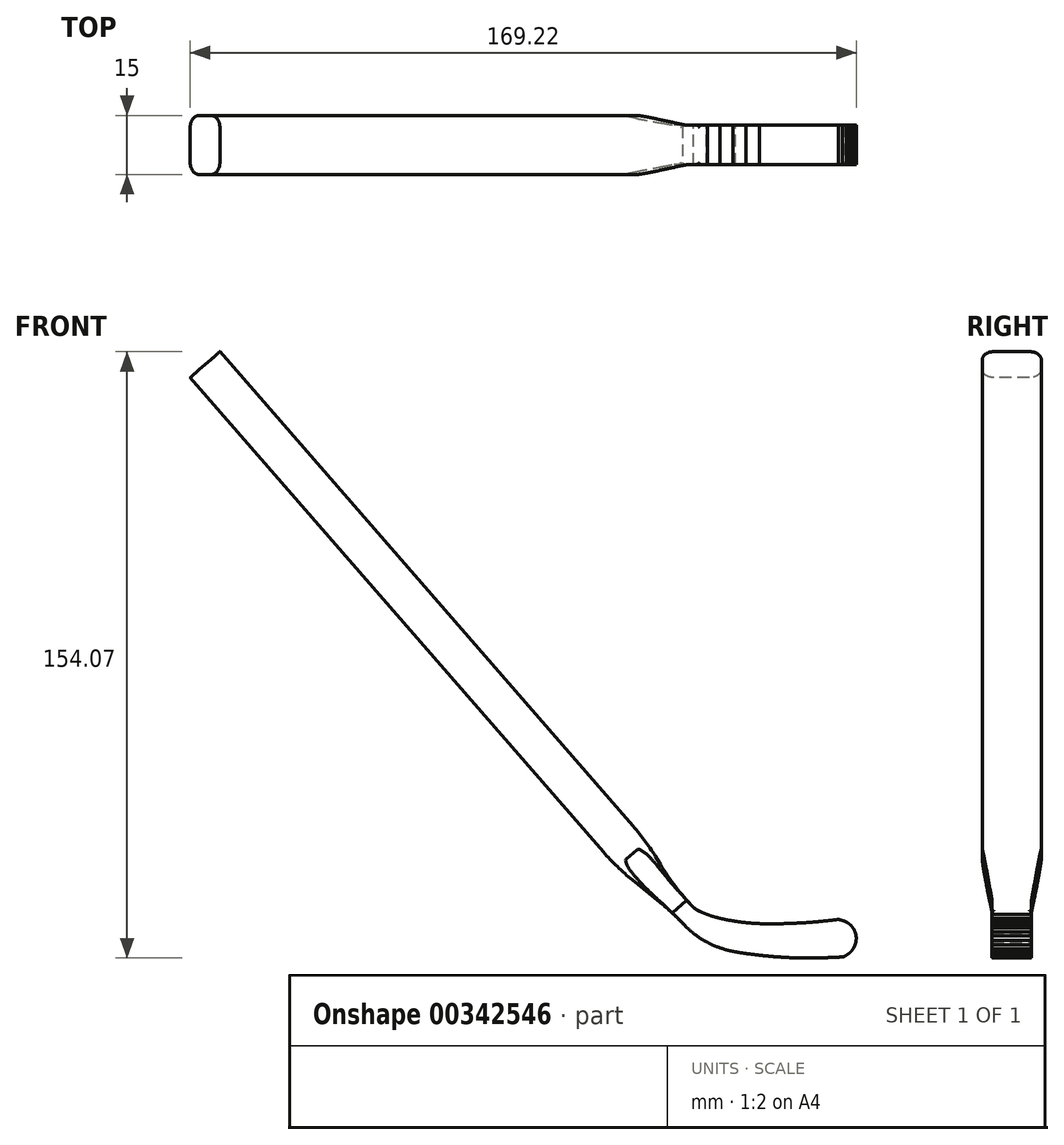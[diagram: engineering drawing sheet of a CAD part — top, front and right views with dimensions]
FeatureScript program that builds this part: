
annotation { "Feature Type Name" : "Feature", "Feature Type Description" : "" }
export const myFeature = defineFeature(function(context is Context, id is Id, definition is map)
    precondition{}
    {
        {
            var Q0;
            Q0=qCreatedBy(makeId("Front.planeOp"),FACE);
            var sketch = newSketch(context, id + "F0", { "sketchPlane" : qUnion([Q0])});
            skFitSpline(sketch, "E0.0", {"points": [v(-96.58, 20.1) * mm, v(-97.72, 20.03) * mm, v(-98.88, 19.98) * mm, v(-100.04, 19.94) * mm]});
            skFitSpline(sketch, "E1.0", {"points": [v(-93.22, 20.32) * mm, v(-94.31, 20.23) * mm, v(-95.44, 20.15) * mm, v(-96.58, 20.1) * mm]});
            skFitSpline(sketch, "E2.0", {"points": [v(-90.02, 20.62) * mm, v(-91.06, 20.51) * mm, v(-92.12, 20.4) * mm, v(-93.22, 20.32) * mm]});
            skFitSpline(sketch, "E3.0", {"points": [v(-86.91, 20.97) * mm, v(-87.3, 20.93) * mm, v(-87.69, 20.88) * mm, v(-88.72, 20.77) * mm, v(-89.5, 20.68) * mm, v(-90.02, 20.62) * mm]});
            skFitSpline(sketch, "E4.0", {"points": [v(-123.3, 23.6) * mm, v(-123.8, 23.85) * mm, v(-124.54, 24.24) * mm, v(-125.52, 24.78) * mm, v(-125.9, 24.98) * mm, v(-126.26, 25.18) * mm]});
            skFitSpline(sketch, "E5.0", {"points": [v(-120.24, 22.25) * mm, v(-121.28, 22.64) * mm, v(-122.3, 23.1) * mm, v(-123.3, 23.6) * mm]});
            skFitSpline(sketch, "E6.0", {"points": [v(-117.03, 21.27) * mm, v(-118.12, 21.54) * mm, v(-119.2, 21.85) * mm, v(-120.24, 22.25) * mm]});
            skFitSpline(sketch, "E7.0", {"points": [v(-113.73, 20.61) * mm, v(-114.84, 20.8) * mm, v(-115.94, 21) * mm, v(-117.03, 21.27) * mm]});
            skFitSpline(sketch, "E8.0", {"points": [v(-110.37, 20.17) * mm, v(-111.5, 20.28) * mm, v(-112.61, 20.43) * mm, v(-113.73, 20.61) * mm]});
            skFitSpline(sketch, "E9.0", {"points": [v(-106.97, 19.92) * mm, v(-108.11, 19.97) * mm, v(-109.25, 20.05) * mm, v(-110.37, 20.17) * mm]});
            skFitSpline(sketch, "E10.0", {"points": [v(-103.52, 19.86) * mm, v(-104.68, 19.86) * mm, v(-105.83, 19.87) * mm, v(-106.97, 19.92) * mm]});
            skFitSpline(sketch, "E11.0", {"points": [v(-100.04, 19.94) * mm, v(-101.2, 19.9) * mm, v(-102.36, 19.87) * mm, v(-103.52, 19.86) * mm]});
            skFitSpline(sketch, "E12.0", {"points": [v(-93.11, 11.2) * mm, v(-91.83, 11.2) * mm, v(-90.58, 11.24) * mm, v(-89.35, 11.29) * mm]});
            skFitSpline(sketch, "E13.0", {"points": [v(-89.35, 11.29) * mm, v(-88.73, 11.3) * mm, v(-87.82, 11.35) * mm, v(-86.6, 11.4) * mm, v(-86.15, 11.42) * mm, v(-85.7, 11.44) * mm]});
            skFitSpline(sketch, "E14.0", {"points": [v(-97.05, 11.21) * mm, v(-95.71, 11.18) * mm, v(-94.4, 11.18) * mm, v(-93.11, 11.2) * mm]});
            skFitSpline(sketch, "E15.0", {"points": [v(-101.09, 11.38) * mm, v(-99.73, 11.3) * mm, v(-98.38, 11.24) * mm, v(-97.05, 11.21) * mm]});
            skFitSpline(sketch, "E16.0", {"points": [v(-105.14, 11.7) * mm, v(-103.8, 11.57) * mm, v(-102.44, 11.46) * mm, v(-101.09, 11.38) * mm]});
            skFitSpline(sketch, "E17.0", {"points": [v(-109.17, 12.15) * mm, v(-107.84, 11.98) * mm, v(-106.5, 11.83) * mm, v(-105.14, 11.7) * mm]});
            skFitSpline(sketch, "E18.0", {"points": [v(-113.12, 12.76) * mm, v(-111.83, 12.5) * mm, v(-110.5, 12.32) * mm, v(-109.17, 12.15) * mm]});
            skFitSpline(sketch, "E19.0", {"points": [v(-116.92, 13.73) * mm, v(-115.7, 13.32) * mm, v(-114.42, 13) * mm, v(-113.12, 12.76) * mm]});
            skFitSpline(sketch, "E20.0", {"points": [v(-120.48, 15.3) * mm, v(-119.34, 14.68) * mm, v(-118.15, 14.15) * mm, v(-116.92, 13.73) * mm]});
            skFitSpline(sketch, "E21.0", {"points": [v(-123.73, 17.45) * mm, v(-122.7, 16.64) * mm, v(-121.62, 15.92) * mm, v(-120.48, 15.3) * mm]});
            skFitSpline(sketch, "E22.0", {"points": [v(-126.63, 20.09) * mm, v(-125.7, 19.15) * mm, v(-124.75, 18.26) * mm, v(-123.73, 17.45) * mm]});
            skFitSpline(sketch, "E23.0", {"points": [v(-129.33, 22.99) * mm, v(-129, 22.62) * mm, v(-128.66, 22.25) * mm, v(-127.77, 21.27) * mm, v(-127.09, 20.56) * mm, v(-126.63, 20.09) * mm]});
            skFitSpline(sketch, "E24.0", {"points": [v(-85.87, 20.69) * mm, v(-86.04, 20.74) * mm, v(-86.3, 20.81) * mm, v(-86.65, 20.9) * mm, v(-86.78, 20.94) * mm, v(-86.91, 20.97) * mm]});
            skFitSpline(sketch, "E25.0", {"points": [v(-84.88, 20.28) * mm, v(-85.2, 20.45) * mm, v(-85.53, 20.58) * mm, v(-85.87, 20.69) * mm]});
            skFitSpline(sketch, "E26.0", {"points": [v(-84, 19.66) * mm, v(-84.27, 19.9) * mm, v(-84.56, 20.11) * mm, v(-84.88, 20.28) * mm]});
            skFitSpline(sketch, "E27.0", {"points": [v(-83.27, 18.84) * mm, v(-83.48, 19.15) * mm, v(-83.73, 19.42) * mm, v(-84, 19.66) * mm]});
            skFitSpline(sketch, "E28.0", {"points": [v(-82.74, 17.86) * mm, v(-82.88, 18.21) * mm, v(-83.06, 18.54) * mm, v(-83.27, 18.84) * mm]});
            skFitSpline(sketch, "E29.0", {"points": [v(-82.46, 16.77) * mm, v(-82.51, 17.15) * mm, v(-82.6, 17.51) * mm, v(-82.74, 17.86) * mm]});
            skFitSpline(sketch, "E30.0", {"points": [v(-82.46, 15.65) * mm, v(-82.42, 16.02) * mm, v(-82.41, 16.4) * mm, v(-82.46, 16.77) * mm]});
            skFitSpline(sketch, "E31.0", {"points": [v(-82.72, 14.55) * mm, v(-82.6, 14.9) * mm, v(-82.5, 15.27) * mm, v(-82.46, 15.65) * mm]});
            skFitSpline(sketch, "E32.0", {"points": [v(-83.21, 13.54) * mm, v(-83.01, 13.85) * mm, v(-82.85, 14.2) * mm, v(-82.72, 14.55) * mm]});
            skFitSpline(sketch, "E33.0", {"points": [v(-83.9, 12.68) * mm, v(-83.65, 12.93) * mm, v(-83.41, 13.22) * mm, v(-83.21, 13.54) * mm]});
            skFitSpline(sketch, "E34.0", {"points": [v(-84.76, 12) * mm, v(-84.46, 12.2) * mm, v(-84.17, 12.43) * mm, v(-83.9, 12.68) * mm]});
            skFitSpline(sketch, "E35.0", {"points": [v(-85.7, 11.44) * mm, v(-85.57, 11.51) * mm, v(-85.45, 11.58) * mm, v(-85.14, 11.77) * mm, v(-84.9, 11.9) * mm, v(-84.76, 12) * mm]});
            skLineSegment(sketch, "E36", {"start": v(-126.26, 25.18) * mm, "end": v(-129.09, 22.72) * mm});
            skSolve(sketch);
        }
        {
            var Q0;
            Q0=makeQuery(id+"F0.imprint","IMPRINT",FACE,{"disambiguationData":[TD([[makeQuery(id+"F0.imprint","IMPRINT",EDGE,{"derivedFrom":sQuery(id+"F0.wireOp",EDGE,"E0.0")}),1.0]])]});
            extrude(context, id + "F1", {"entities" : qUnion([Q0]), "depth" : 10 * mm});
        }
        {
            var Q0;
            Q0=makeQuery(id+"F1.opExtrude","SWEPT_FACE",FACE,{"disambiguationData":[OSD([sQuery(id+"F0.wireOp",EDGE,"E36")])]});
            cPlane(context, id + "F2", {"entities" : qUnion([Q0]), "cplaneType" : CPlaneType.OFFSET, "offset" : 18 * mm, "width" : 150 * mm, "height" : 150 * mm});
        }
        {
            var Q0;
            Q0=qCreatedBy(id+"F2.planeOp",FACE);
            var sketch = newSketch(context, id + "F3", { "sketchPlane" : qUnion([Q0])});
            skLineSegment(sketch, "E37.0", {"start": v(-78.68, -10) * mm, "end": v(-78.68, 0) * mm});
            skLineSegment(sketch, "E38.0", {"start": v(-78.68, -10) * mm, "end": v(-82.43, -10) * mm, "construction": true});
            skPoint(sketch, "E39", {"position": v(-80.56, -5) * mm});
            skPoint(sketch, "E39.positionSnap0", {"position": v(-80.56, -10) * mm});
            skPoint(sketch, "E39.positionSnap1", {"position": v(-78.68, -5) * mm});
            skLineSegment(sketch, "E40.bottom", {"start": v(-75.56, 2.5) * mm, "end": v(-85.56, 2.5) * mm});
            skLineSegment(sketch, "E40.top", {"start": v(-75.56, -12.5) * mm, "end": v(-85.56, -12.5) * mm});
            skLineSegment(sketch, "E40.left", {"start": v(-75.56, 2.5) * mm, "end": v(-75.56, -12.5) * mm});
            skLineSegment(sketch, "E40.right", {"start": v(-85.56, 2.5) * mm, "end": v(-85.56, -12.5) * mm});
            skSolve(sketch);
        }
        {
            var Q0;
            Q0=makeQuery(id+"F3.imprint","IMPRINT",FACE,{"disambiguationData":[TD([[makeQuery(id+"F3.imprint","IMPRINT",EDGE,{"derivedFrom":sQuery(id+"F3.wireOp",EDGE,"E40.bottom")}),1.0]])]});
            extrude(context, id + "F4", {"entities" : qUnion([Q0]), "depth" : 165 * mm});
        }
        {
            var Q0;
            Q0=makeQuery(id+"F4.opExtrude","CAP_FACE",FACE,{"disambiguationData":[OSD([sQuery(id+"F3.wireOp",EDGE,"E40.bottom"),sQuery(id+"F3.wireOp",EDGE,"E40.top"),sQuery(id+"F3.wireOp",EDGE,"E40.left"),sQuery(id+"F3.wireOp",EDGE,"E40.right")])],"isStart":true});
            var Q1;
            Q1=makeQuery(id+"F1.opExtrude","SWEPT_FACE",FACE,{"disambiguationData":[OSD([sQuery(id+"F0.wireOp",EDGE,"E36")])]});
            loft(context, id + "F5", {"sheetProfilesArray" : [{ "sheetProfileEntities" : qUnion([Q0]) }, { "sheetProfileEntities" : qUnion([Q1]) }]});
        }
        {
            var Q0;
            Q0=makeQuery(id+"F1.opExtrude","SWEPT_BODY",BODY,{"disambiguationData":[OSD([sQuery(id+"F0.wireOp",EDGE,"E0.0"),sQuery(id+"F0.wireOp",EDGE,"E1.0"),sQuery(id+"F0.wireOp",EDGE,"E2.0"),sQuery(id+"F0.wireOp",EDGE,"E3.0"),sQuery(id+"F0.wireOp",EDGE,"E4.0"),sQuery(id+"F0.wireOp",EDGE,"E5.0"),sQuery(id+"F0.wireOp",EDGE,"E6.0"),sQuery(id+"F0.wireOp",EDGE,"E7.0"),sQuery(id+"F0.wireOp",EDGE,"E8.0"),sQuery(id+"F0.wireOp",EDGE,"E9.0"),sQuery(id+"F0.wireOp",EDGE,"E10.0"),sQuery(id+"F0.wireOp",EDGE,"E11.0"),sQuery(id+"F0.wireOp",EDGE,"E12.0"),sQuery(id+"F0.wireOp",EDGE,"E13.0"),sQuery(id+"F0.wireOp",EDGE,"E14.0"),sQuery(id+"F0.wireOp",EDGE,"E15.0"),sQuery(id+"F0.wireOp",EDGE,"E16.0"),sQuery(id+"F0.wireOp",EDGE,"E17.0"),sQuery(id+"F0.wireOp",EDGE,"E18.0"),sQuery(id+"F0.wireOp",EDGE,"E19.0"),sQuery(id+"F0.wireOp",EDGE,"E20.0"),sQuery(id+"F0.wireOp",EDGE,"E21.0"),sQuery(id+"F0.wireOp",EDGE,"E22.0"),sQuery(id+"F0.wireOp",EDGE,"E23.0"),sQuery(id+"F0.wireOp",EDGE,"E24.0"),sQuery(id+"F0.wireOp",EDGE,"E25.0"),sQuery(id+"F0.wireOp",EDGE,"E26.0"),sQuery(id+"F0.wireOp",EDGE,"E27.0"),sQuery(id+"F0.wireOp",EDGE,"E28.0"),sQuery(id+"F0.wireOp",EDGE,"E29.0"),sQuery(id+"F0.wireOp",EDGE,"E30.0"),sQuery(id+"F0.wireOp",EDGE,"E31.0"),sQuery(id+"F0.wireOp",EDGE,"E32.0"),sQuery(id+"F0.wireOp",EDGE,"E33.0"),sQuery(id+"F0.wireOp",EDGE,"E34.0"),sQuery(id+"F0.wireOp",EDGE,"E35.0"),sQuery(id+"F0.wireOp",EDGE,"E36")])]});
            var Q1;
            Q1=makeQuery(id+"F5.opLoft","SWEPT_BODY",BODY,{"disambiguationData":[OSD([sQuery(id+"F0.wireOp",EDGE,"E36"),sQuery(id+"F3.wireOp",EDGE,"E40.bottom"),sQuery(id+"F3.wireOp",EDGE,"E40.top"),sQuery(id+"F3.wireOp",EDGE,"E40.left"),sQuery(id+"F3.wireOp",EDGE,"E40.right")])]});
            var Q2;
            Q2=makeQuery(id+"F4.opExtrude","SWEPT_BODY",BODY,{"disambiguationData":[OSD([sQuery(id+"F3.wireOp",EDGE,"E40.bottom"),sQuery(id+"F3.wireOp",EDGE,"E40.top"),sQuery(id+"F3.wireOp",EDGE,"E40.left"),sQuery(id+"F3.wireOp",EDGE,"E40.right")])]});
            booleanBodies(context, id + "F6", {"operationType" : BooleanOperationType.UNION, "tools" : qUnion([Q0, Q1, Q2])});
        }
        {
            var Q0;
            {var subQ0=sQuery(id+"F0.wireOp",EDGE,"E36");var subQ1=sQuery(id+"F0.wireOp",EDGE,"E4.0");Q0=makeQuery(id+"F6.opBoolean","MERGE",EDGE,{"derivedFrom":[makeQuery(id+"F1.opExtrude","SWEPT_EDGE",EDGE,{"disambiguationData":[OSD([subQ1,subQ0])]}),makeQuery(id+"F5.opLoft","MID_CAP_EDGE",EDGE,{"disambiguationData":[OSD([subQ1,subQ0])],"capPos":1.0})]});}
            var Q1;
            {var subQ0=sQuery(id+"F3.wireOp",EDGE,"E40.left");Q1=makeQuery(id+"F6.opBoolean","MERGE",EDGE,{"derivedFrom":[makeQuery(id+"F4.opExtrude","CAP_EDGE",EDGE,{"disambiguationData":[OSD([subQ0])],"isStart":true}),makeQuery(id+"F5.opLoft","MID_CAP_EDGE",EDGE,{"disambiguationData":[OSD([sQuery(id+"F3.wireOp",EDGE,"E40.bottom"),sQuery(id+"F3.wireOp",EDGE,"E40.top"),subQ0])],"capPos":0.0})]});}
            var Q2;
            {var subQ0=sQuery(id+"F0.wireOp",EDGE,"E36");var subQ1=sQuery(id+"F0.wireOp",EDGE,"E23.0");Q2=makeQuery(id+"F6.opBoolean","MERGE",EDGE,{"derivedFrom":[makeQuery(id+"F1.opExtrude","SWEPT_EDGE",EDGE,{"disambiguationData":[OSD([subQ1,subQ0])]}),makeQuery(id+"F5.opLoft","MID_CAP_EDGE",EDGE,{"disambiguationData":[OSD([subQ1,subQ0])],"capPos":1.0})]});}
            var Q3;
            {var subQ0=sQuery(id+"F3.wireOp",EDGE,"E40.right");Q3=makeQuery(id+"F6.opBoolean","MERGE",EDGE,{"derivedFrom":[makeQuery(id+"F4.opExtrude","CAP_EDGE",EDGE,{"disambiguationData":[OSD([subQ0])],"isStart":true}),makeQuery(id+"F5.opLoft","MID_CAP_EDGE",EDGE,{"disambiguationData":[OSD([sQuery(id+"F3.wireOp",EDGE,"E40.bottom"),sQuery(id+"F3.wireOp",EDGE,"E40.top"),subQ0])],"capPos":0.0})]});}
            fillet(context, id + "F7", {"entities" : qUnion([Q0, Q1, Q2, Q3]), "radius" : 60 * mm, "tangentPropagation" : true, "allowEdgeOverflow" : false});
        }
        {
            var Q0;
            {var subQ0=sQuery(id+"F0.wireOp",EDGE,"E36");var subQ1=sQuery(id+"F0.wireOp",EDGE,"E4.0");Q0=makeQuery(id+"F7.opFillet","BLEND_EDGE",EDGE,{"blendedFrom":[makeQuery(id+"F6.opBoolean","MERGE",EDGE,{"derivedFrom":[makeQuery(id+"F1.opExtrude","SWEPT_EDGE",EDGE,{"disambiguationData":[OSD([subQ1,subQ0])]}),makeQuery(id+"F5.opLoft","MID_CAP_EDGE",EDGE,{"disambiguationData":[OSD([subQ1,subQ0])],"capPos":1.0})]}),makeQuery(id+"F1.opExtrude","SWEPT_FACE",FACE,{"disambiguationData":[OSD([sQuery(id+"F0.wireOp",EDGE,"E5.0")])]})],"blendedInto":[makeQuery(id+"F1.opExtrude","SWEPT_FACE",FACE,{"disambiguationData":[OSD([sQuery(id+"F0.wireOp",EDGE,"E5.0")])]})]});}
            fillet(context, id + "F8", {"entities" : qUnion([Q0]), "radius" : 5 * mm, "tangentPropagation" : true, "allowEdgeOverflow" : false});
        }
        {
            var Q0;
            Q0=makeQuery(id+"F4.opExtrude","SWEPT_EDGE",EDGE,{"disambiguationData":[OSD([sQuery(id+"F3.wireOp",EDGE,"E40.top"),sQuery(id+"F3.wireOp",EDGE,"E40.left")])]});
            var Q1;
            Q1=makeQuery(id+"F4.opExtrude","SWEPT_EDGE",EDGE,{"disambiguationData":[OSD([sQuery(id+"F3.wireOp",EDGE,"E40.bottom"),sQuery(id+"F3.wireOp",EDGE,"E40.left")])]});
            var Q2;
            Q2=makeQuery(id+"F4.opExtrude","SWEPT_EDGE",EDGE,{"disambiguationData":[OSD([sQuery(id+"F3.wireOp",EDGE,"E40.top"),sQuery(id+"F3.wireOp",EDGE,"E40.right")])]});
            var Q3;
            Q3=makeQuery(id+"F4.opExtrude","SWEPT_EDGE",EDGE,{"disambiguationData":[OSD([sQuery(id+"F3.wireOp",EDGE,"E40.bottom"),sQuery(id+"F3.wireOp",EDGE,"E40.right")])]});
            fillet(context, id + "F9", {"entities" : qUnion([Q0, Q1, Q2, Q3]), "radius" : 3 * mm, "tangentPropagation" : true, "allowEdgeOverflow" : false});
        }
    });
